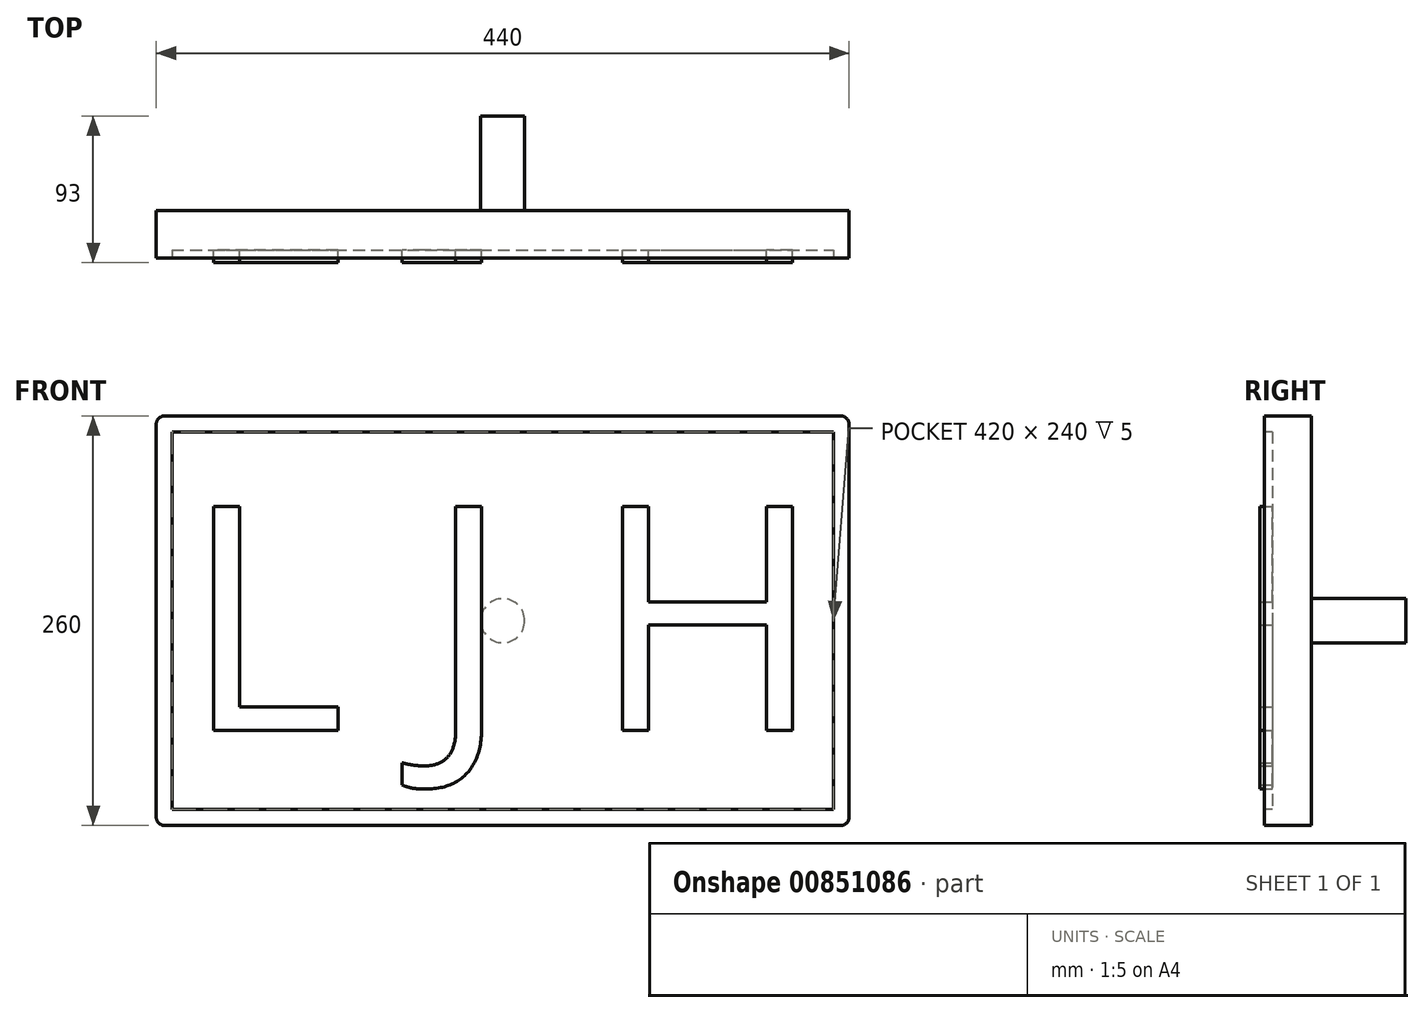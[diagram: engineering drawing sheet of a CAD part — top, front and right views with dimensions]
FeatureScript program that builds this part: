
annotation { "Feature Type Name" : "Feature", "Feature Type Description" : "" }
export const myFeature = defineFeature(function(context is Context, id is Id, definition is map)
    precondition{}
    {
        {
            var Q0;
            Q0=qCreatedBy(makeId("Front.planeOp"),FACE);
            var sketch = newSketch(context, id + "F0", { "sketchPlane" : qUnion([Q0])});
            skLineSegment(sketch, "E0.bottom", {"start": v(-70, 40) * mm, "end": v(370, 40) * mm});
            skLineSegment(sketch, "E0.top", {"start": v(-70, -220) * mm, "end": v(370, -220) * mm});
            skLineSegment(sketch, "E0.left", {"start": v(-70, 40) * mm, "end": v(-70, -220) * mm});
            skLineSegment(sketch, "E0.right", {"start": v(370, 40) * mm, "end": v(370, -220) * mm});
            skSolve(sketch);
        }
        {
            var Q0;
            Q0=makeQuery(id+"F0.imprint","IMPRINT",FACE,{"disambiguationData":[TD([[makeQuery(id+"F0.imprint","IMPRINT",EDGE,{"derivedFrom":sQuery(id+"F0.wireOp",EDGE,"E0.bottom")}),-1.0]])]});
            extrude(context, id + "F1", {"entities" : qUnion([Q0]), "depth" : 30 * mm, "offsetDistance" : 25 * mm});
        }
        {
            var Q0;
            Q0=makeQuery(id+"F1.opExtrude","SWEPT_EDGE",EDGE,{"disambiguationData":[OSD([sQuery(id+"F0.wireOp",EDGE,"E0.bottom"),sQuery(id+"F0.wireOp",EDGE,"E0.left")])]});
            var Q1;
            Q1=makeQuery(id+"F1.opExtrude","SWEPT_EDGE",EDGE,{"disambiguationData":[OSD([sQuery(id+"F0.wireOp",EDGE,"E0.top"),sQuery(id+"F0.wireOp",EDGE,"E0.left")])]});
            var Q2;
            Q2=makeQuery(id+"F1.opExtrude","SWEPT_EDGE",EDGE,{"disambiguationData":[OSD([sQuery(id+"F0.wireOp",EDGE,"E0.bottom"),sQuery(id+"F0.wireOp",EDGE,"E0.right")])]});
            var Q3;
            Q3=makeQuery(id+"F1.opExtrude","SWEPT_EDGE",EDGE,{"disambiguationData":[OSD([sQuery(id+"F0.wireOp",EDGE,"E0.top"),sQuery(id+"F0.wireOp",EDGE,"E0.right")])]});
            fillet(context, id + "F2", {"entities" : qUnion([Q0, Q1, Q2, Q3]), "radius" : 5 * mm, "tangentPropagation" : true, "allowEdgeOverflow" : false});
        }
        {
            var Q0;
            Q0=makeQuery(id+"F1.opExtrude","CAP_FACE",FACE,{"disambiguationData":[OSD([sQuery(id+"F0.wireOp",EDGE,"E0.bottom"),sQuery(id+"F0.wireOp",EDGE,"E0.top"),sQuery(id+"F0.wireOp",EDGE,"E0.left"),sQuery(id+"F0.wireOp",EDGE,"E0.right")])],"isStart":false});
            var sketch = newSketch(context, id + "F3", { "sketchPlane" : qUnion([Q0])});
            skLineSegment(sketch, "E1.bottom", {"start": v(-60, 30) * mm, "end": v(360, 30) * mm});
            skLineSegment(sketch, "E1.top", {"start": v(-60, -210) * mm, "end": v(360, -210) * mm});
            skLineSegment(sketch, "E1.left", {"start": v(-60, 30) * mm, "end": v(-60, -210) * mm});
            skLineSegment(sketch, "E1.right", {"start": v(360, 30) * mm, "end": v(360, -210) * mm});
            skSolve(sketch);
        }
        {
            var Q0;
            Q0=makeQuery(id+"F3.imprint","IMPRINT",FACE,{"disambiguationData":[TD([[makeQuery(id+"F3.imprint","IMPRINT",EDGE,{"derivedFrom":sQuery(id+"F3.wireOp",EDGE,"E1.bottom")}),-1.0]])]});
            extrude(context, id + "F4", {"entities" : qUnion([Q0]), "operationType" : NewBodyOperationType.REMOVE, "oppositeDirection" : true, "depth" : 5 * mm, "offsetDistance" : 25 * mm});
        }
        {
            var Q0;
            Q0=makeQuery(id+"F1.opExtrude","CAP_FACE",FACE,{"disambiguationData":[OSD([sQuery(id+"F0.wireOp",EDGE,"E0.bottom"),sQuery(id+"F0.wireOp",EDGE,"E0.top"),sQuery(id+"F0.wireOp",EDGE,"E0.left"),sQuery(id+"F0.wireOp",EDGE,"E0.right")])],"isStart":true});
            var sketch = newSketch(context, id + "F5", { "sketchPlane" : qUnion([Q0])});
            skCircle(sketch, "E2", {"center": v(-150, -90) * mm, "radius": 14 * mm});
            skPoint(sketch, "E2.centerSnap0", {"position": v(70, -90) * mm});
            skPoint(sketch, "E2.centerSnap1", {"position": v(-150, 40) * mm});
            skSolve(sketch);
        }
        {
            var Q0;
            Q0=makeQuery(id+"F5.imprint","IMPRINT",FACE,{"disambiguationData":[TD([[makeQuery(id+"F5.imprint","IMPRINT",EDGE,{"derivedFrom":sQuery(id+"F5.wireOp",EDGE,"bM4MkmcM-94eN-VAaA-9p6Q-aXGfnGZ8u9RH")}),1.0]])]});
            var Q1;
            Q1=makeQuery(id+"F5.imprint","IMPRINT",FACE,{"disambiguationData":[TD([[makeQuery(id+"F5.imprint","IMPRINT",EDGE,{"derivedFrom":sQuery(id+"F5.wireOp",EDGE,"E2")}),1.0]])]});
            extrude(context, id + "F6", {"entities" : qUnion([Q0, Q1]), "operationType" : NewBodyOperationType.ADD, "depth" : 60 * mm, "offsetDistance" : 25 * mm});
        }
        {
            var Q0;
            Q0=qCreatedBy(makeId("Front.planeOp"),FACE);
            var sketch = newSketch(context, id + "F7", { "sketchPlane" : qUnion([Q0])});
            skText(sketch, "E3", { "text": "L J H", "fontName": "OpenSans-Regular.ttf"});
            const initialGuessF7  = {"E3": [-0.05319, -0.15957, 1, 0, 0.14323]};
            skSetInitialGuess(sketch, initialGuessF7);
            skSolve(sketch);
        }
        {
            var Q0;
            Q0 = qSketchRegion(id + "F7", true);
            extrude(context, id + "F8", {"entities" : qUnion([Q0]), "depth" : 33 * mm, "offsetDistance" : 25 * mm});
        }
        {
            var Q0;
            Q0=makeQuery(id+"F1.opExtrude","SWEPT_BODY",BODY,{"disambiguationData":[OSD([sQuery(id+"F0.wireOp",EDGE,"E0.bottom"),sQuery(id+"F0.wireOp",EDGE,"E0.top"),sQuery(id+"F0.wireOp",EDGE,"E0.left"),sQuery(id+"F0.wireOp",EDGE,"E0.right")])]});
            var Q1;
            Q1=makeQuery(id+"F8.opExtrude","SWEPT_BODY",BODY,{"disambiguationData":[OSD([sQuery(id+"F7.wireOp",EDGE,"E3.sketch_text.stroke-0"),sQuery(id+"F7.wireOp",EDGE,"E3.sketch_text.stroke-1"),sQuery(id+"F7.wireOp",EDGE,"E3.sketch_text.stroke-2"),sQuery(id+"F7.wireOp",EDGE,"E3.sketch_text.stroke-3"),sQuery(id+"F7.wireOp",EDGE,"E3.sketch_text.stroke-4"),sQuery(id+"F7.wireOp",EDGE,"E3.sketch_text.stroke-5")])]});
            var Q2;
            Q2=makeQuery(id+"F8.opExtrude","SWEPT_BODY",BODY,{"disambiguationData":[OSD([sQuery(id+"F7.wireOp",EDGE,"E3.sketch_text.stroke-6"),sQuery(id+"F7.wireOp",EDGE,"E3.sketch_text.stroke-7"),sQuery(id+"F7.wireOp",EDGE,"E3.sketch_text.stroke-8"),sQuery(id+"F7.wireOp",EDGE,"E3.sketch_text.stroke-9"),sQuery(id+"F7.wireOp",EDGE,"E3.sketch_text.stroke-10"),sQuery(id+"F7.wireOp",EDGE,"E3.sketch_text.stroke-11"),sQuery(id+"F7.wireOp",EDGE,"E3.sketch_text.stroke-12"),sQuery(id+"F7.wireOp",EDGE,"E3.sketch_text.stroke-13"),sQuery(id+"F7.wireOp",EDGE,"E3.sketch_text.stroke-14"),sQuery(id+"F7.wireOp",EDGE,"E3.sketch_text.stroke-15")])]});
            var Q3;
            Q3=makeQuery(id+"F8.opExtrude","SWEPT_BODY",BODY,{"disambiguationData":[OSD([sQuery(id+"F7.wireOp",EDGE,"E3.sketch_text.stroke-16"),sQuery(id+"F7.wireOp",EDGE,"E3.sketch_text.stroke-17"),sQuery(id+"F7.wireOp",EDGE,"E3.sketch_text.stroke-18"),sQuery(id+"F7.wireOp",EDGE,"E3.sketch_text.stroke-19"),sQuery(id+"F7.wireOp",EDGE,"E3.sketch_text.stroke-20"),sQuery(id+"F7.wireOp",EDGE,"E3.sketch_text.stroke-21"),sQuery(id+"F7.wireOp",EDGE,"E3.sketch_text.stroke-22"),sQuery(id+"F7.wireOp",EDGE,"E3.sketch_text.stroke-23"),sQuery(id+"F7.wireOp",EDGE,"E3.sketch_text.stroke-24"),sQuery(id+"F7.wireOp",EDGE,"E3.sketch_text.stroke-25"),sQuery(id+"F7.wireOp",EDGE,"E3.sketch_text.stroke-26"),sQuery(id+"F7.wireOp",EDGE,"E3.sketch_text.stroke-27")])]});
            booleanBodies(context, id + "F9", {"operationType" : BooleanOperationType.SUBTRACTION, "tools" : qUnion([Q0]), "targets" : qUnion([Q1, Q2, Q3]), "keepTools" : true});
        }
    });
